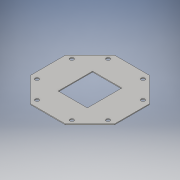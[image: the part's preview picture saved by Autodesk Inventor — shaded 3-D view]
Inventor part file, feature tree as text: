
AUTODESK INVENTOR PART (.ipt)
format: ipt  version: 2016 (Build 200138000, 138)  size: 125,952 bytes
history: native  units: in
note: dims shown in document units (in); Inventor stores cm internally (conversion verified against a paired STEP export)
features: extrude x3, sketch x3
ambient origin geometry x8: Origin, YZ Plane, XZ Plane, XY Plane, X Axis, Y Axis, Z Axis, Center Point
bodies: Solid1 (feature_tree)
feature tree (6):
  extrude  "Extrusion1"  TaperAngle=67.5deg  [1 undecoded]
  extrude  "Extrusion2"  Depth=0.0625in TaperAngle=0.0deg
  extrude  "Extrusion3"  Depth=2.65in
  sketch  "Sketch1"  dims[d0=7.0in d1=67.5deg]
  sketch  "Sketch2"  dims[d2=6.4672in d3=0.0625in d4=0.0in]
  sketch  "Sketch3"  dims[d5=2.25in d6=2.65in d7=0.0625in d8=0.0in d9=0.285in d10=0.5in d11=0.0in d12=1.5748in d14=360.0deg d16=0.0625in d17=0.0in]
note: 1 required parameter value undecoded (feature->parameter linkage not recoverable at this tier; creation-order binding heuristic only, values carry confidence <= 0.55)
